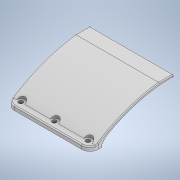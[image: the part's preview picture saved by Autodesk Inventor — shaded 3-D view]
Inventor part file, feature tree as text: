
AUTODESK INVENTOR PART (.ipt)
format: ipt  version: 2020 (Build 240168000, 168)  size: 253,440 bytes
history: native  units: in
note: dims shown in document units (in); Inventor stores cm internally (conversion verified against a paired STEP export)
features: extrude x4, sketch x4, fillet x3
ambient origin geometry x8: Origin, YZ Plane, XZ Plane, XY Plane, X Axis, Y Axis, Z Axis, Center Point
bodies: Solid1 (feature_tree)
feature tree (11):
  extrude  "Extrusion1"  Depth=4.0in
  extrude  "Extrusion2"  Depth=0.2in
  extrude  "Extrusion3"  Depth=0.12in
  extrude  "Extrusion4"  Depth=0.04in
  fillet  "Fillet1"  Radius=0.15in
  fillet  "Fillet2"  Radius=4.0in
  fillet  "Fillet3"  Radius=0.4in
  sketch  "Sketch1"  dims[d0=4.0in d1=4.0in]
  sketch  "Sketch2"  dims[d2=1.3in d3=0.0in d4=0.2in]
  sketch  "Sketch3"  dims[d5=0.3in d6=0.12in]
  sketch  "Sketch4"  dims[d7=0.15in d8=0.7in d9=0.15in d10=4.0in d11=0.0in d12=0.4in d13=0.4in d14=0.4in d15=0.4in d16=0.4in d17=4.0in d18=0.0in d19=0.4in d20=0.4in d21=0.2in d22=0.2in d23=0.2in d24=0.2in d25=4.0in d26=0.0in d27=0.4in d28=0.05in d29=0.04in]
